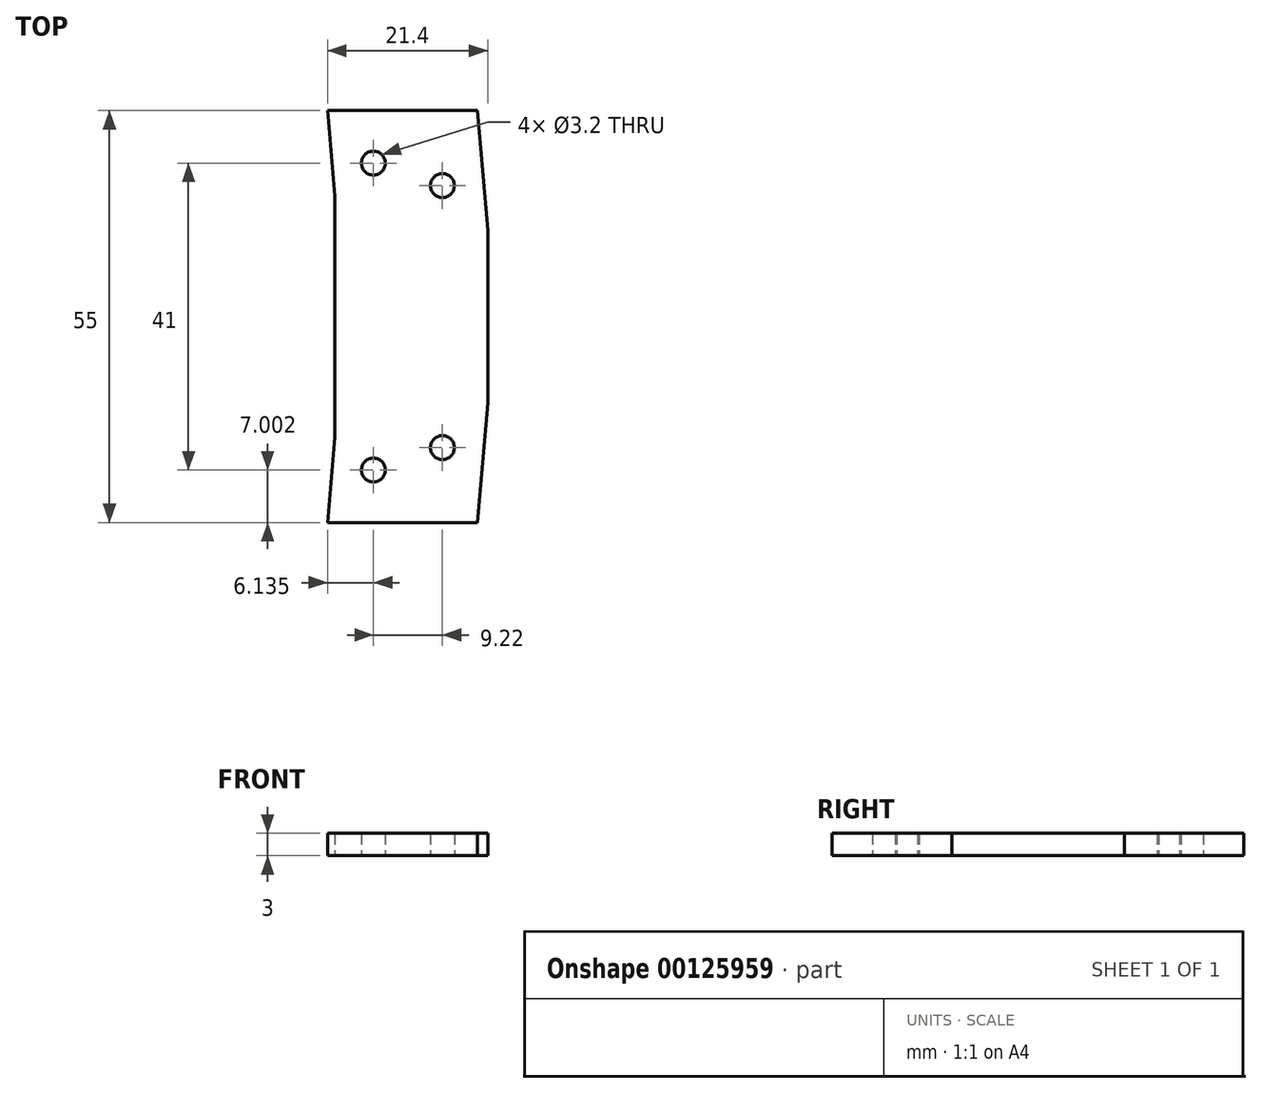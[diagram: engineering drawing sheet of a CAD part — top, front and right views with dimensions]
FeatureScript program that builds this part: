
annotation { "Feature Type Name" : "Feature", "Feature Type Description" : "" }
export const myFeature = defineFeature(function(context is Context, id is Id, definition is map)
    precondition{}
    {
        {
            var Q0;
            Q0=qCreatedBy(makeId("Top.planeOp"),FACE);
            var sketch = newSketch(context, id + "F0", { "sketchPlane" : qUnion([Q0])});
            skCircle(sketch, "E0", {"center": v(-17.3, 43.73) * mm, "radius": 1.6 * mm});
            skCircle(sketch, "E1", {"center": v(-8.08, 40.73) * mm, "radius": 1.6 * mm});
            skCircle(sketch, "E2", {"center": v(-17.3, 2.73) * mm, "radius": 1.6 * mm});
            skCircle(sketch, "E3", {"center": v(-8.08, 5.73) * mm, "radius": 1.6 * mm});
            skLineSegment(sketch, "E4", {"start": v(-23.44, 50.73) * mm, "end": v(-3.44, 50.73) * mm});
            skLineSegment(sketch, "E5", {"start": v(-3.44, -4.27) * mm, "end": v(-23.44, -4.27) * mm});
            skLineSegment(sketch, "E6", {"start": v(-3.44, -4.27) * mm, "end": v(-2.04, 11.73) * mm});
            skLineSegment(sketch, "E7", {"start": v(-2.04, 11.73) * mm, "end": v(-2.04, 34.73) * mm});
            skLineSegment(sketch, "E8", {"start": v(-2.04, 34.73) * mm, "end": v(-3.44, 50.73) * mm});
            skLineSegment(sketch, "E9", {"start": v(-23.44, -4.27) * mm, "end": v(-22.44, 7.12) * mm});
            skLineSegment(sketch, "E10", {"start": v(-23.44, 50.73) * mm, "end": v(-22.44, 39.34) * mm});
            skLineSegment(sketch, "E11", {"start": v(-22.44, 39.34) * mm, "end": v(-22.44, 7.12) * mm});
            skSolve(sketch);
        }
        {
            var Q0;
            Q0=makeQuery(id+"F0.imprint","IMPRINT",FACE,{"disambiguationData":[TD([[makeQuery(id+"F0.imprint","IMPRINT",EDGE,{"derivedFrom":sQuery(id+"F0.wireOp",EDGE,"E0")}),-1.0]])]});
            var Q1;
            Q1=makeQuery(id+"F0.imprint","IMPRINT",FACE,{"disambiguationData":[TD([[makeQuery(id+"F0.imprint","IMPRINT",EDGE,{"derivedFrom":sQuery(id+"F0.wireOp",EDGE,"ulm2NCjs-PCS1-cfSD-3naN-ud7H9mVaTFHX")}),1.0]])]});
            extrude(context, id + "F1", {"entities" : qUnion([Q0, Q1]), "depth" : 3 * mm});
        }
    });
